# Revit family: Magnuson-DDF-Coat_Rack-
name_source: partatom
category: Furniture
revit_build: Autodesk Revit 2014 (Build: 20130308_1515(x64)
units: mm (PartAtom-declared; Revit-internal decimal feet)

## types (3) — shared parameters
Assembly Code = E2020200
Cap = MG - Black Plastic
Depth = 18 3/8"
Frame = MG - Steel, Wrought
Hanger Rod = MG - Black Plastic
Height = 61"
Keynote = 12500
Low Emitting Finish = Yes
Low Emitting Material = Yes
Manufacturer = MAGNUSON
Model = 3D-DDF-3H
Salvage or Reuse = Yes
Shelf = MG - Steel, Wrought
Type Comments = DS
URL = www.magnusongroup.com
zero-valued in all types: Percentage of Recycled Content

## per-type parameters (varying)
| type | Description | Width |
| 3D-DDF-3H | 36W Double Sided Steel Floor Rack With Hanger Rod | 36" |
| 3D-DDF-4H | 48W Double Sided Steel Floor Rack With Hanger Rod | 48" |
| 3D-DDF-5H | 60W Double Sided Steel Floor Rack With Hanger Rod | 60" |

## geometry (parser evidence)
native form markers: Sweep x1
no freeform markers — native parametric forms only
